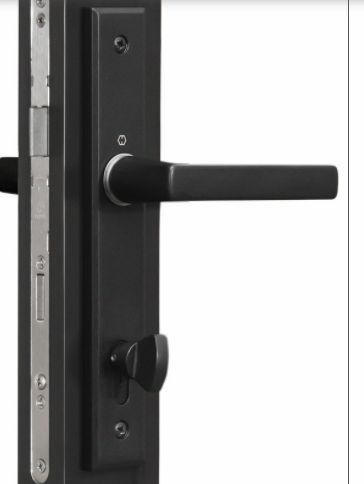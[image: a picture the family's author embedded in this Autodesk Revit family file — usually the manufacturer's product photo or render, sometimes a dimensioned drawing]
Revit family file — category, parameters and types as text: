
# Revit family: Door_Swing_Aluminum_WesternWindow_7900-Double
name_source: partatom
category: Doors
revit_build: Autodesk Revit 2015 (Build: 20140606_1530(x64)
units: mm (PartAtom-declared; Revit-internal decimal feet)

## types (2) — shared parameters
AAMA Designation = as Specified
Air Infiltration = as Specified
Analytic Construction = <None>
Fire Rating = As Specified
Flip Nailing Fin = No
Frame Depth = 0' - 5 7/8"
Function = Interior
Heat Transfer Coefficient (U) = 1 BTU/(h·ft²·°F)
Keynote = 08 11 00
Manufacturer = Western Window Systems
Manufacturer Fax = 602-243-3119
Manufacturer Website = https://www.westernwindowsystems.com
Maximum Size = as Specified
Miami Dade Conformance = as Specified
Model = 900 Hinged Door
Operation = as Specified
Panel Thickness = 0' - 2 1/4"
Product Data = http://www.arcat.com
Product Properties = https://www.westernwindowsystems.com
R = 0.0000 (h·ft²·°F)/BTU
RO Offset = 0' - 0 1/2"
Revision = R1_2018-02
Sales Information = https://www.westernwindowsystems.com
Standards Conformance = as Specified
Structural Test Pressure = as Specified
Thermal Resistance (R) = 0.0000 (h·ft²·°F)/BTU
Thickness = 0' - 0"
U = 1 BTU/(h·ft²·°F)
URL = https://www.westernwindowsystems.com
Wall Closure = By host
Water Penetration = as Specified
zero-valued in all types: Expected Lifespan (Years), Maintenance Schedule (Months), SHGC, Solar Heat Gain Coefficient, VLT, Visual Light Transmittance, Warranty Duration (Years)

## per-type parameters (varying)
| type | Description | Inswing | Outswing |
| Inswing | Western Window Aluminum Pair Inswing Door - 7900 as Specified | Yes | No |
| Outswing | Western Window Aluminum Pair Outswing Door - 7900 as Specified | No | Yes |

## geometry (parser evidence)
native form markers: Sweep x15
no freeform markers — native parametric forms only
